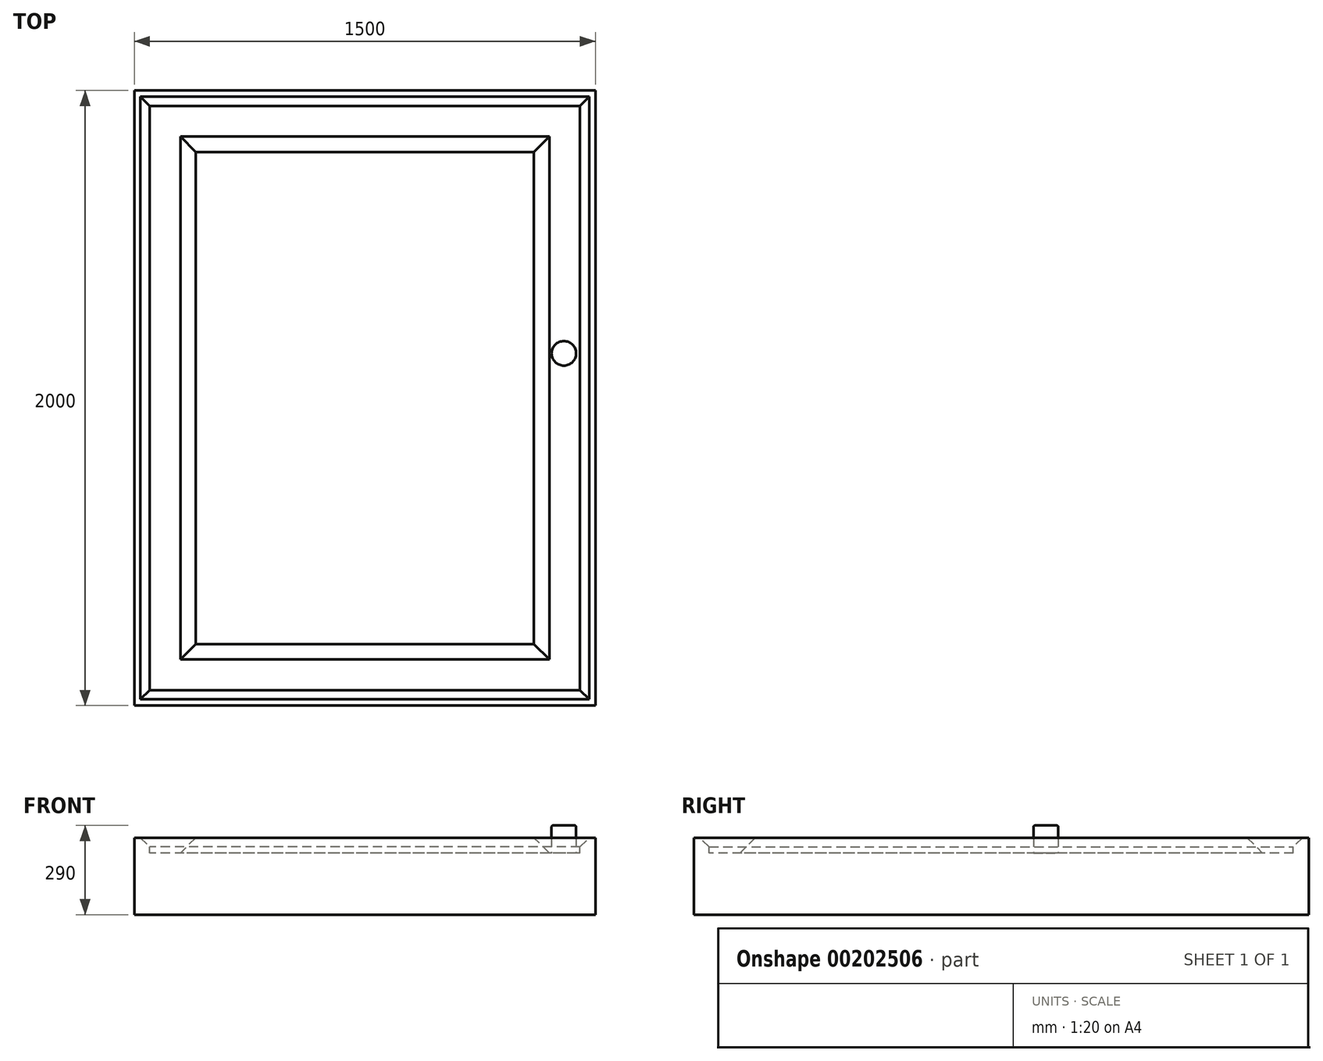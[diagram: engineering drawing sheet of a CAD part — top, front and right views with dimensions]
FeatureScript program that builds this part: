
annotation { "Feature Type Name" : "Feature", "Feature Type Description" : "" }
export const myFeature = defineFeature(function(context is Context, id is Id, definition is map)
    precondition{}
    {
        {
            var Q0;
            Q0=qCreatedBy(makeId("Top.planeOp"),FACE);
            var sketch = newSketch(context, id + "F0", { "sketchPlane" : qUnion([Q0])});
            skLineSegment(sketch, "E0.bottom", {"start": v(750, 1000) * mm, "end": v(-750, 1000) * mm});
            skLineSegment(sketch, "E0.top", {"start": v(750, -1000) * mm, "end": v(-750, -1000) * mm});
            skLineSegment(sketch, "E0.left", {"start": v(750, 1000) * mm, "end": v(750, -1000) * mm});
            skLineSegment(sketch, "E0.right", {"start": v(-750, 1000) * mm, "end": v(-750, -1000) * mm});
            skPoint(sketch, "E0.middle", {"position": v(0, 0) * mm});
            skLineSegment(sketch, "E1.bottom", {"start": v(700, 950) * mm, "end": v(-700, 950) * mm});
            skLineSegment(sketch, "E1.top", {"start": v(700, -950) * mm, "end": v(-700, -950) * mm});
            skLineSegment(sketch, "E1.left", {"start": v(700, 950) * mm, "end": v(700, -950) * mm});
            skLineSegment(sketch, "E1.right", {"start": v(-700, 950) * mm, "end": v(-700, -950) * mm});
            skLineSegment(sketch, "E2.bottom", {"start": v(600, 850) * mm, "end": v(-600, 850) * mm});
            skLineSegment(sketch, "E2.top", {"start": v(600, -850) * mm, "end": v(-600, -850) * mm});
            skLineSegment(sketch, "E2.left", {"start": v(600, 850) * mm, "end": v(600, -850) * mm});
            skLineSegment(sketch, "E2.right", {"start": v(-600, 850) * mm, "end": v(-600, -850) * mm});
            skSolve(sketch);
        }
        {
            var Q0;
            Q0=makeQuery(id+"F0.imprint","IMPRINT",FACE,{"disambiguationData":[TD([[makeQuery(id+"F0.imprint","IMPRINT",EDGE,{"derivedFrom":sQuery(id+"F0.wireOp",EDGE,"E0.bottom")}),1.0]])]});
            var Q1;
            Q1=makeQuery(id+"F0.imprint","IMPRINT",FACE,{"disambiguationData":[TD([[makeQuery(id+"F0.imprint","IMPRINT",EDGE,{"derivedFrom":sQuery(id+"F0.wireOp",EDGE,"E2.bottom")}),1.0]])]});
            var Q2;
            Q2=makeQuery(id+"F0.imprint","IMPRINT",FACE,{"disambiguationData":[TD([[makeQuery(id+"F0.imprint","IMPRINT",EDGE,{"derivedFrom":sQuery(id+"F0.wireOp",EDGE,"E1.bottom")}),1.0]])]});
            extrude(context, id + "F1", {"entities" : qUnion([Q0, Q1, Q2]), "endBound" : BoundingType.SYMMETRIC, "depth" : 250 * mm});
        }
        {
            var Q0;
            Q0=makeQuery(id+"F1.opExtrude","CAP_FACE",FACE,{"disambiguationData":[OSD([sQuery(id+"F0.wireOp",EDGE,"E0.bottom"),sQuery(id+"F0.wireOp",EDGE,"E0.top"),sQuery(id+"F0.wireOp",EDGE,"E0.left"),sQuery(id+"F0.wireOp",EDGE,"E0.right")])],"isStart":false});
            var sketch = newSketch(context, id + "F2", { "sketchPlane" : qUnion([Q0])});
            skLineSegment(sketch, "E3.bottom", {"start": v(700, 950) * mm, "end": v(-700, 950) * mm});
            skLineSegment(sketch, "E3.top", {"start": v(700, -950) * mm, "end": v(-700, -950) * mm});
            skLineSegment(sketch, "E3.left", {"start": v(700, 950) * mm, "end": v(700, -950) * mm});
            skLineSegment(sketch, "E3.right", {"start": v(-700, 950) * mm, "end": v(-700, -950) * mm});
            skPoint(sketch, "E3.middle", {"position": v(0, 0) * mm});
            skLineSegment(sketch, "E4.bottom", {"start": v(600, 850) * mm, "end": v(-600, 850) * mm});
            skLineSegment(sketch, "E4.top", {"start": v(600, -850) * mm, "end": v(-600, -850) * mm});
            skLineSegment(sketch, "E4.left", {"start": v(600, 850) * mm, "end": v(600, -850) * mm});
            skLineSegment(sketch, "E4.right", {"start": v(-600, 850) * mm, "end": v(-600, -850) * mm});
            skSolve(sketch);
        }
        {
            var Q0;
            Q0=makeQuery(id+"F2.imprint","IMPRINT",FACE,{"disambiguationData":[TD([[makeQuery(id+"F2.imprint","IMPRINT",EDGE,{"derivedFrom":sQuery(id+"F2.wireOp",EDGE,"E3.bottom")}),1.0]])]});
            extrude(context, id + "F3", {"entities" : qUnion([Q0]), "operationType" : NewBodyOperationType.REMOVE, "oppositeDirection" : true, "depth" : 50 * mm});
        }
        {
            var Q0;
            Q0=makeQuery(id+"F3.boolean.opBoolean","COPY",EDGE,{"derivedFrom":makeQuery(id+"F3.opExtrude","CAP_EDGE",EDGE,{"disambiguationData":[OSD([sQuery(id+"F2.wireOp",EDGE,"E4.right")])],"isStart":true})});
            var Q1;
            Q1=makeQuery(id+"F3.boolean.opBoolean","SPLIT",FACE,{"disambiguationData":[TD([makeQuery(id+"F3.opExtrude","SWEPT_FACE",FACE,{"disambiguationData":[OSD([sQuery(id+"F2.wireOp",EDGE,"E4.bottom")])]})])],"derivedFrom":makeQuery(id+"F1.opExtrude","CAP_FACE",FACE,{"disambiguationData":[OSD([sQuery(id+"F0.wireOp",EDGE,"E0.bottom"),sQuery(id+"F0.wireOp",EDGE,"E0.top"),sQuery(id+"F0.wireOp",EDGE,"E0.left"),sQuery(id+"F0.wireOp",EDGE,"E0.right")])],"isStart":false})});
            chamfer(context, id + "F4", {"entities" : qUnion([Q0, Q1]), "width" : 50 * mm, "tangentPropagation" : true});
        }
        {
            var Q0;
            Q0=makeQuery(id+"F3.boolean.opBoolean","COPY",EDGE,{"derivedFrom":makeQuery(id+"F3.opExtrude","CAP_EDGE",EDGE,{"disambiguationData":[OSD([sQuery(id+"F2.wireOp",EDGE,"E3.right")])],"isStart":true})});
            var Q1;
            Q1=makeQuery(id+"F3.boolean.opBoolean","COPY",EDGE,{"derivedFrom":makeQuery(id+"F3.opExtrude","CAP_EDGE",EDGE,{"disambiguationData":[OSD([sQuery(id+"F2.wireOp",EDGE,"E3.bottom")])],"isStart":true})});
            var Q2;
            Q2=makeQuery(id+"F3.boolean.opBoolean","COPY",EDGE,{"derivedFrom":makeQuery(id+"F3.opExtrude","CAP_EDGE",EDGE,{"disambiguationData":[OSD([sQuery(id+"F2.wireOp",EDGE,"E3.left")])],"isStart":true})});
            var Q3;
            Q3=makeQuery(id+"F3.boolean.opBoolean","COPY",EDGE,{"derivedFrom":makeQuery(id+"F3.opExtrude","CAP_EDGE",EDGE,{"disambiguationData":[OSD([sQuery(id+"F2.wireOp",EDGE,"E3.top")])],"isStart":true})});
            chamfer(context, id + "F5", {"entities" : qUnion([Q0, Q1, Q2, Q3]), "width" : 30 * mm, "tangentPropagation" : true});
        }
        {
            var Q0;
            Q0=makeQuery(id+"F3.boolean.opBoolean","COPY",FACE,{"derivedFrom":makeQuery(id+"F3.opExtrude","CAP_FACE",FACE,{"disambiguationData":[OSD([sQuery(id+"F2.wireOp",EDGE,"E3.bottom"),sQuery(id+"F2.wireOp",EDGE,"E3.top"),sQuery(id+"F2.wireOp",EDGE,"E3.left"),sQuery(id+"F2.wireOp",EDGE,"E3.right"),sQuery(id+"F2.wireOp",EDGE,"E4.bottom"),sQuery(id+"F2.wireOp",EDGE,"E4.top"),sQuery(id+"F2.wireOp",EDGE,"E4.left"),sQuery(id+"F2.wireOp",EDGE,"E4.right")])],"isStart":false})});
            var sketch = newSketch(context, id + "F6", { "sketchPlane" : qUnion([Q0])});
            skCircle(sketch, "E5", {"center": v(647.29, 145.27) * mm, "radius": 40 * mm});
            skSolve(sketch);
        }
        {
            var Q0;
            Q0=makeQuery(id+"F6.imprint","IMPRINT",FACE,{"disambiguationData":[TD([[makeQuery(id+"F6.imprint","IMPRINT",EDGE,{"derivedFrom":sQuery(id+"F6.wireOp",EDGE,"E5")}),1.0]])]});
            extrude(context, id + "F7", {"entities" : qUnion([Q0]), "operationType" : NewBodyOperationType.ADD, "depth" : 90 * mm});
        }
        {
            var Q0;
            Q0=makeQuery(id+"F7.opExtrude","CAP_EDGE",EDGE,{"disambiguationData":[OSD([sQuery(id+"F6.wireOp",EDGE,"E5")])],"isStart":false});
            fillet(context, id + "F8", {"entities" : qUnion([Q0]), "radius" : 5 * mm, "tangentPropagation" : true, "allowEdgeOverflow" : false});
        }
    });
